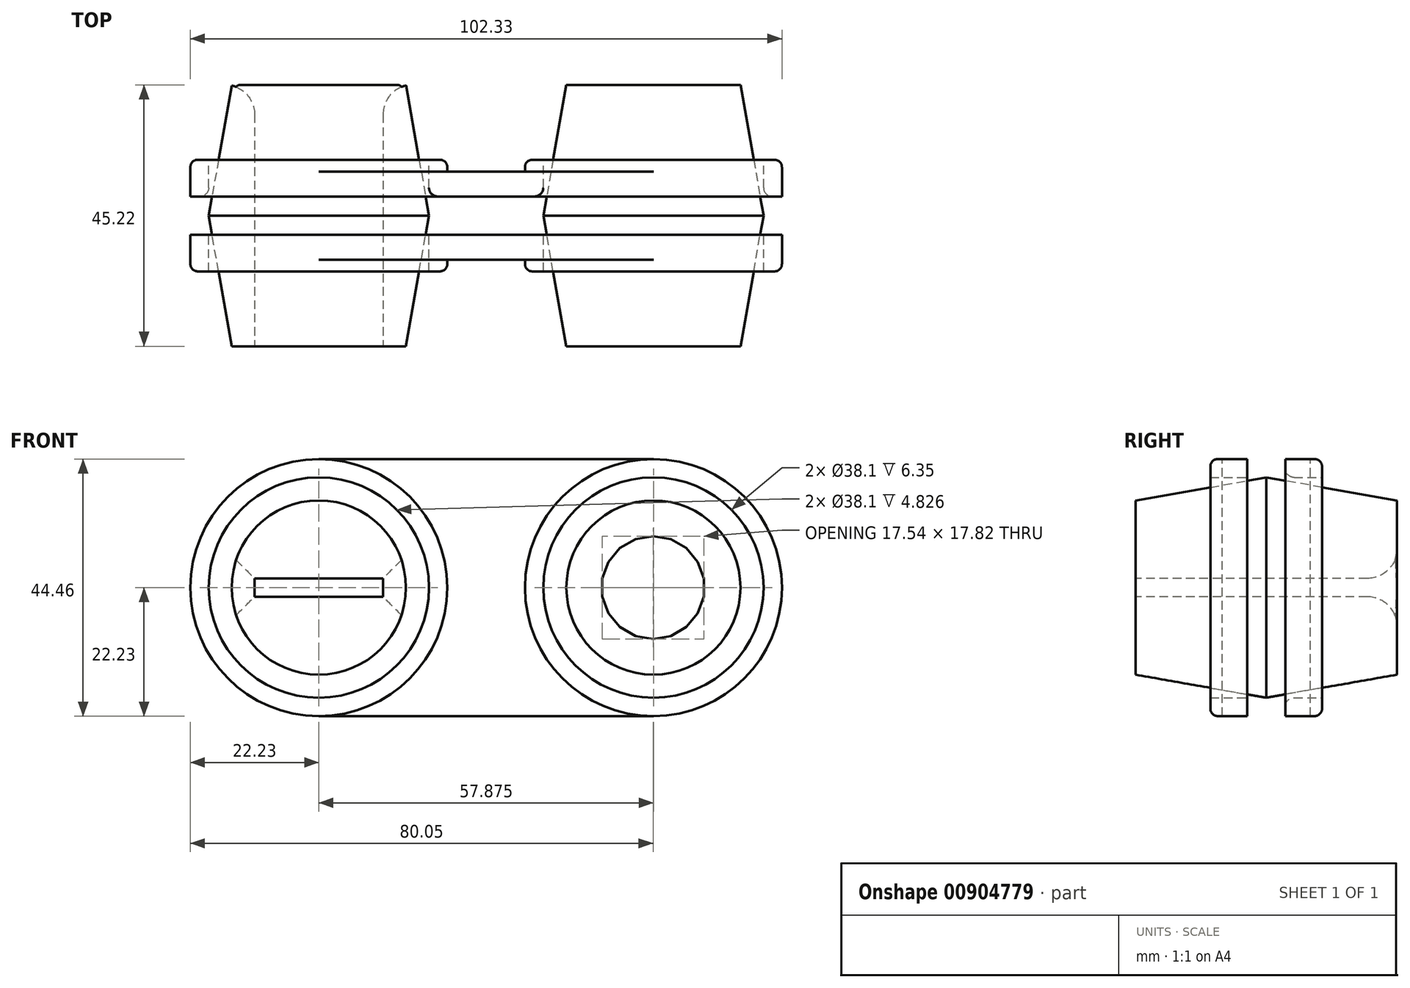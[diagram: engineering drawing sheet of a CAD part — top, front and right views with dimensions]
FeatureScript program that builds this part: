
annotation { "Feature Type Name" : "Feature", "Feature Type Description" : "" }
export const myFeature = defineFeature(function(context is Context, id is Id, definition is map)
    precondition{}
    {
        {
            var Q0;
            Q0=qCreatedBy(makeId("Front.planeOp"),FACE);
            var sketch = newSketch(context, id + "F0", { "sketchPlane" : qUnion([Q0])});
            skCircle(sketch, "E0", {"center": v(0, 0) * mm, "radius": 22.22 * mm});
            skCircle(sketch, "E1", {"center": v(57.88, 0) * mm, "radius": 22.22 * mm});
            skLineSegment(sketch, "E2", {"start": v(0, 22.22) * mm, "end": v(57.88, 22.22) * mm});
            skLineSegment(sketch, "E3", {"start": v(0, -22.22) * mm, "end": v(57.88, -22.22) * mm});
            skCircle(sketch, "E4", {"center": v(0, 0) * mm, "radius": 19.05 * mm});
            skCircle(sketch, "E5", {"center": v(57.88, 0) * mm, "radius": 19.05 * mm});
            skSolve(sketch);
        }
        {
            var Q0;
            Q0=makeQuery(id+"F0.imprint","IMPRINT",FACE,{"disambiguationData":[TD([[makeQuery(id+"F0.imprint","IMPRINT",EDGE,{"derivedFrom":sQuery(id+"F0.wireOp",EDGE,"E4")}),-1.0]])]});
            var Q1;
            Q1=makeQuery(id+"F0.imprint","IMPRINT",FACE,{"disambiguationData":[TD([[makeQuery(id+"F0.imprint","IMPRINT",EDGE,{"derivedFrom":sQuery(id+"F0.wireOp",EDGE,"E5")}),-1.0]])]});
            extrude(context, id + "F1", {"entities" : qUnion([Q0, Q1]), "depth" : 9.65 * mm, "offsetDistance" : 25.4 * mm});
        }
        {
            var Q0;
            {var subQ0=sQuery(id+"F0.wireOp",EDGE,"E2");Q0=makeQuery(id+"F0.imprint","IMPRINT",FACE,{"disambiguationData":[TD([[makeQuery(id+"F0.imprint","IMPRINT",EDGE,{"derivedFrom":subQ0}),-1.0]])]});}
            extrude(context, id + "F2", {"entities" : qUnion([Q0]), "endBound" : BoundingType.SYMMETRIC, "depth" : 15.24 * mm, "offsetDistance" : 25.4 * mm});
        }
        {
            var Q0;
            Q0=makeQuery(id+"F1.opExtrude","SWEPT_BODY",BODY,{"disambiguationData":[OSD([sQuery(id+"F0.wireOp",EDGE,"E0"),sQuery(id+"F0.wireOp",EDGE,"E4")])]});
            var Q1;
            Q1=makeQuery(id+"F1.opExtrude","SWEPT_BODY",BODY,{"disambiguationData":[OSD([sQuery(id+"F0.wireOp",EDGE,"E1"),sQuery(id+"F0.wireOp",EDGE,"E5")])]});
            var Q2;
            {var subQ0=sQuery(id+"F0.wireOp",EDGE,"E2");Q2=makeQuery(id+"F0.imprint","IMPRINT",FACE,{"disambiguationData":[TD([[makeQuery(id+"F0.imprint","IMPRINT",EDGE,{"derivedFrom":subQ0}),-1.0]])]});}
            mirror(context, id + "F3", {"operationType" : NewBodyOperationType.ADD, "entities" : qUnion([Q0, Q1]), "mirrorPlane" : qUnion([Q2])});
        }
        {
            var Q0;
            Q0 = qSketchRegion(id + "F0", true);
            extrude(context, id + "F4", {"entities" : qUnion([Q0]), "operationType" : NewBodyOperationType.REMOVE, "endBound" : BoundingType.SYMMETRIC, "depth" : 6.6 * mm, "offsetDistance" : 25.4 * mm});
        }
        {
            var Q0;
            Q0=makeQuery(id+"F1.opExtrude","CAP_EDGE",EDGE,{"disambiguationData":[OSD([sQuery(id+"F0.wireOp",EDGE,"E0")])],"isStart":false});
            var Q1;
            Q1=makeQuery(id+"F1.opExtrude","CAP_EDGE",EDGE,{"disambiguationData":[OSD([sQuery(id+"F0.wireOp",EDGE,"E1")])],"isStart":false});
            var Q2;
            Q2=makeQuery(id+"F3.opPattern","COPY",EDGE,{"derivedFrom":makeQuery(id+"F1.opExtrude","CAP_EDGE",EDGE,{"disambiguationData":[OSD([sQuery(id+"F0.wireOp",EDGE,"E1")])],"isStart":false}),"instanceName":"1"});
            var Q3;
            Q3=makeQuery(id+"F3.opPattern","COPY",EDGE,{"derivedFrom":makeQuery(id+"F1.opExtrude","CAP_EDGE",EDGE,{"disambiguationData":[OSD([sQuery(id+"F0.wireOp",EDGE,"E0")])],"isStart":false}),"instanceName":"1"});
            fillet(context, id + "F5", {"entities" : qUnion([Q0, Q1, Q2, Q3]), "radius" : 1.27 * mm, "tangentPropagation" : true, "allowEdgeOverflow" : false});
        }
        {
            var Q0;
            Q0=makeQuery(id+"F0.imprint","IMPRINT",FACE,{"disambiguationData":[TD([[makeQuery(id+"F0.imprint","IMPRINT",EDGE,{"derivedFrom":sQuery(id+"F0.wireOp",EDGE,"E5")}),1.0]])]});
            var Q1;
            Q1=makeQuery(id+"F0.imprint","IMPRINT",FACE,{"disambiguationData":[TD([[makeQuery(id+"F0.imprint","IMPRINT",EDGE,{"derivedFrom":sQuery(id+"F0.wireOp",EDGE,"E4")}),1.0]])]});
            var Q2;
            Q2=sQuery(id+"F0.wireOp",EDGE,"E5");
            var Q3;
            Q3=sQuery(id+"F0.wireOp",EDGE,"E4");
            extrude(context, id + "F6", {"entities" : qUnion([Q0, Q1]), "surfaceEntities" : qUnion([Q2, Q3]), "endBound" : BoundingType.SYMMETRIC, "depth" : 45.2 * mm, "offsetDistance" : 25.4 * mm, "hasDraft" : true, "draftAngle" : 10 * degree, "draftPullDirection" : true});
        }
        {
            var Q0;
            Q0=makeQuery(id+"F4.boolean.opBoolean","COPY",EDGE,{"derivedFrom":makeQuery(id+"F4.opExtrude","CAP_EDGE",EDGE,{"disambiguationData":[OSD([sQuery(id+"F0.wireOp",EDGE,"E5")])],"isStart":true})});
            var Q1;
            Q1=makeQuery(id+"F4.boolean.opBoolean","COPY",EDGE,{"derivedFrom":makeQuery(id+"F4.opExtrude","CAP_EDGE",EDGE,{"disambiguationData":[OSD([sQuery(id+"F0.wireOp",EDGE,"E5")])],"isStart":false})});
            var Q2;
            Q2=makeQuery(id+"F4.boolean.opBoolean","COPY",EDGE,{"derivedFrom":makeQuery(id+"F4.opExtrude","CAP_EDGE",EDGE,{"disambiguationData":[OSD([sQuery(id+"F0.wireOp",EDGE,"E4")])],"isStart":false})});
            var Q3;
            Q3=makeQuery(id+"F4.boolean.opBoolean","COPY",EDGE,{"derivedFrom":makeQuery(id+"F4.opExtrude","CAP_EDGE",EDGE,{"disambiguationData":[OSD([sQuery(id+"F0.wireOp",EDGE,"E4")])],"isStart":true})});
            fillet(context, id + "F7", {"entities" : qUnion([Q0, Q1, Q2, Q3]), "radius" : 1.52 * mm, "tangentPropagation" : true, "allowEdgeOverflow" : false});
        }
        {
            var Q0;
            Q0=makeQuery(id+"F6.opExtrude","CAP_FACE",FACE,{"disambiguationData":[OSD([sQuery(id+"F0.wireOp",EDGE,"E4")])],"isStart":false});
            var sketch = newSketch(context, id + "F8", { "sketchPlane" : qUnion([Q0])});
            skLineSegment(sketch, "E6.bottom", {"start": v(11.11, -1.59) * mm, "end": v(-11.11, -1.59) * mm});
            skLineSegment(sketch, "E6.top", {"start": v(11.11, 1.59) * mm, "end": v(-11.11, 1.59) * mm});
            skLineSegment(sketch, "E6.left", {"start": v(11.11, -1.59) * mm, "end": v(11.11, 1.59) * mm});
            skLineSegment(sketch, "E6.right", {"start": v(-11.11, -1.59) * mm, "end": v(-11.11, 1.59) * mm});
            skPoint(sketch, "E6.middle", {"position": v(0, 0) * mm});
            skCircle(sketch, "E7.cCircle", {"center": v(57.82, 0) * mm, "radius": 8.77 * mm, "construction": true});
            skLineSegment(sketch, "E7.0", {"start": v(66.6, 1.55) * mm, "end": v(66.6, -1.55) * mm});
            skLineSegment(sketch, "E7.1", {"start": v(66.6, -1.55) * mm, "end": v(65.53, -4.45) * mm});
            skLineSegment(sketch, "E7.2", {"start": v(65.53, -4.45) * mm, "end": v(63.55, -6.82) * mm});
            skLineSegment(sketch, "E7.3", {"start": v(63.55, -6.82) * mm, "end": v(60.87, -8.37) * mm});
            skLineSegment(sketch, "E7.4", {"start": v(60.87, -8.37) * mm, "end": v(57.82, -8.9) * mm});
            skLineSegment(sketch, "E7.5", {"start": v(57.82, -8.9) * mm, "end": v(54.77, -8.37) * mm});
            skLineSegment(sketch, "E7.6", {"start": v(54.77, -8.37) * mm, "end": v(52.1, -6.82) * mm});
            skLineSegment(sketch, "E7.7", {"start": v(52.1, -6.82) * mm, "end": v(50.1, -4.45) * mm});
            skLineSegment(sketch, "E7.8", {"start": v(50.1, -4.45) * mm, "end": v(49.05, -1.55) * mm});
            skLineSegment(sketch, "E7.9", {"start": v(49.05, -1.55) * mm, "end": v(49.05, 1.55) * mm});
            skLineSegment(sketch, "E7.10", {"start": v(49.05, 1.55) * mm, "end": v(50.1, 4.45) * mm});
            skLineSegment(sketch, "E7.11", {"start": v(50.1, 4.45) * mm, "end": v(52.1, 6.82) * mm});
            skLineSegment(sketch, "E7.12", {"start": v(52.1, 6.82) * mm, "end": v(54.77, 8.37) * mm});
            skLineSegment(sketch, "E7.13", {"start": v(54.77, 8.37) * mm, "end": v(57.82, 8.9) * mm});
            skLineSegment(sketch, "E7.14", {"start": v(57.82, 8.9) * mm, "end": v(60.87, 8.37) * mm});
            skLineSegment(sketch, "E7.15", {"start": v(60.87, 8.37) * mm, "end": v(63.55, 6.82) * mm});
            skLineSegment(sketch, "E7.16", {"start": v(63.55, 6.82) * mm, "end": v(65.53, 4.45) * mm});
            skLineSegment(sketch, "E7.17", {"start": v(65.53, 4.45) * mm, "end": v(66.6, 1.55) * mm});
            skPoint(sketch, "E7.0.midPoint", {"position": v(66.6, 0) * mm});
            skSolve(sketch);
        }
        {
            var Q0;
            Q0 = qSketchRegion(id + "F8", true);
            extrude(context, id + "F9", {"entities" : qUnion([Q0]), "operationType" : NewBodyOperationType.REMOVE, "endBound" : BoundingType.THROUGH_ALL, "oppositeDirection" : true, "depth" : 25.4 * mm, "offsetDistance" : 25.4 * mm});
        }
        {
            var Q0;
            Q0=makeQuery(id+"F9.boolean.opBoolean","COPY",EDGE,{"derivedFrom":makeQuery(id+"F9.opExtrude","CAP_EDGE",EDGE,{"disambiguationData":[OSD([sQuery(id+"F8.wireOp",EDGE,"E6.top")])],"isStart":true})});
            var Q1;
            Q1=makeQuery(id+"F9.boolean.opBoolean","COPY",EDGE,{"derivedFrom":makeQuery(id+"F9.opExtrude","CAP_EDGE",EDGE,{"disambiguationData":[OSD([sQuery(id+"F8.wireOp",EDGE,"E6.bottom")])],"isStart":true})});
            var Q2;
            Q2=makeQuery(id+"F9.boolean.opBoolean","COPY",EDGE,{"derivedFrom":makeQuery(id+"F9.opExtrude","CAP_EDGE",EDGE,{"disambiguationData":[OSD([sQuery(id+"F8.wireOp",EDGE,"E6.right")])],"isStart":true})});
            var Q3;
            Q3=makeQuery(id+"F9.boolean.opBoolean","COPY",EDGE,{"derivedFrom":makeQuery(id+"F9.opExtrude","CAP_EDGE",EDGE,{"disambiguationData":[OSD([sQuery(id+"F8.wireOp",EDGE,"E6.left")])],"isStart":true})});
            var Q4;
            Q4=makeQuery(id+"F9.boolean.opBoolean","INTERSECT",EDGE,{"derivedFrom":[makeQuery(id+"F6.opExtrude","CAP_FACE",FACE,{"disambiguationData":[OSD([sQuery(id+"F0.wireOp",EDGE,"E4")])],"isStart":true}),makeQuery(id+"F9.opExtrude","SWEPT_FACE",FACE,{"disambiguationData":[OSD([sQuery(id+"F8.wireOp",EDGE,"E6.left")])]})]});
            var Q5;
            Q5=makeQuery(id+"F9.boolean.opBoolean","INTERSECT",EDGE,{"derivedFrom":[makeQuery(id+"F6.opExtrude","CAP_FACE",FACE,{"disambiguationData":[OSD([sQuery(id+"F0.wireOp",EDGE,"E4")])],"isStart":true}),makeQuery(id+"F9.opExtrude","SWEPT_FACE",FACE,{"disambiguationData":[OSD([sQuery(id+"F8.wireOp",EDGE,"E6.top")])]})]});
            var Q6;
            Q6=makeQuery(id+"F9.boolean.opBoolean","INTERSECT",EDGE,{"derivedFrom":[makeQuery(id+"F6.opExtrude","CAP_FACE",FACE,{"disambiguationData":[OSD([sQuery(id+"F0.wireOp",EDGE,"E4")])],"isStart":true}),makeQuery(id+"F9.opExtrude","SWEPT_FACE",FACE,{"disambiguationData":[OSD([sQuery(id+"F8.wireOp",EDGE,"E6.bottom")])]})]});
            var Q7;
            Q7=makeQuery(id+"F9.boolean.opBoolean","INTERSECT",EDGE,{"derivedFrom":[makeQuery(id+"F6.opExtrude","CAP_FACE",FACE,{"disambiguationData":[OSD([sQuery(id+"F0.wireOp",EDGE,"E4")])],"isStart":true}),makeQuery(id+"F9.opExtrude","SWEPT_FACE",FACE,{"disambiguationData":[OSD([sQuery(id+"F8.wireOp",EDGE,"E6.right")])]})]});
            fillet(context, id + "F10", {"entities" : qUnion([Q0, Q1, Q2, Q3, Q4, Q5, Q6, Q7]), "radius" : 5.08 * mm, "tangentPropagation" : true, "allowEdgeOverflow" : false});
        }
        {
            var Q0;
            Q0 = qSketchRegion(id + "F8", true);
            extrude(context, id + "F11", {"entities" : qUnion([Q0]), "operationType" : NewBodyOperationType.REMOVE, "endBound" : BoundingType.SYMMETRIC, "depth" : 109.22 * mm, "offsetDistance" : 25.4 * mm});
        }
    });
